SOLIDWORKS PART (.sldprt)
format: sldprt  version: not decoded by parser v0  size: 186,880 bytes
history: native  units: mm
features: plane x3, sketch x3, fillet x2, material x1, revolve x1, extrude x1, cut_extrude x1 (+10 scaffold rows collapsed)
feature tree (22):
  scaffold x10  (default folders/planes/origin — collapsed)
  material  "Matériau <non spécifié>"
  plane  "Plan de face"
  plane  "Plan de dessus"
  plane  "Plan de droite"
  sketch  "Esquisse1"  dims[c1.D1=1.0mm c1.D2=0.3mm c2.D1=~5.727186mm c3.D1=55.0deg c4.D1=~5.860496mm c5.D1=120.0deg]
  revolve  "Révolution1"  Angle=360deg
  sketch  "Esquisse2"  dims[c1.D4=1.0mm c1.D3=1.0mm c1.D1=~10.405565mm c2.D1=118.0deg c2.D2=4.0mm c2.D3=~13.114204mm c3.D3=139.0deg c3.D4=~5.297686mm c4.D3=~2.736869mm c5.D3=139.0deg]
  extrude  "Extrusion1"  Depth=1.2mm
  sketch  "Esquisse3"  dims[D1=1.9mm]
  cut_extrude  "Enlèv. mat.-Extru.1"  [1 undecoded]
  fillet  "Congé11"  Radius=0.6mm
  fillet  "Congé12"  Radius=0.1mm
decode coverage: 7 of 8 modeling features carry decoded parameters
note: ~ marks probable driven/reference dimensions
note: 1 parameter value undecoded
note: suppression state not decoded; provenance and decode notes live in map.json
